# Revit family: 35401-presto
name_source: partatom
category: Plumbing Fixtures
units: mm (PartAtom-declared; Revit-internal decimal feet)

## family parameters
Always vertical = Yes
Cut with Voids When Loaded = No
Maintain Annotation Orientation = No
OmniClass Number = 23.45.00.00
OmniClass Title = Sanitary, Laundry, and Cleaning Equipment
Part Type = Normal
Room Calculation Point = No
Round Connector Dimension = Use Diameter
Shared = No
Work Plane-Based = Yes

## types (1)
- 35401-presto
    - Hydraulic supply = 15.00 mm
    Default Elevation = 1219 mm
    Description = Thermostatic Concealed Shower Mixer TOUCH
    Manufacturer = presto
    Model = 35401
    RANGE = Thermostatic Concealed Shower Mixer TOUCH
    Recommended pressure = 300000.0 Pa
    Ref = 35401 - Timed-flow mixer tap in waterproof box for shower - Battery-operated
    URL = https://www.prestodatashare.com
    brand = LES ROBINETS PRESTO
    flow = 8.0 L/min
    flow time = 30.0 s
    material 1 = Stainless Steel, Polished
    material 2 = Plastic
    material 3 = Bronze, Architectural
    min flow = 6.0 L/min
    min pressure = 100000.0 Pa
    power = 12 W
    pressure = 500000.0 Pa
    ref = 35401 - Timed-flow mixer tap in waterproof box for shower - Battery-operated

## geometry (parser evidence)
native form markers: Sweep x3
no freeform markers — native parametric forms only
